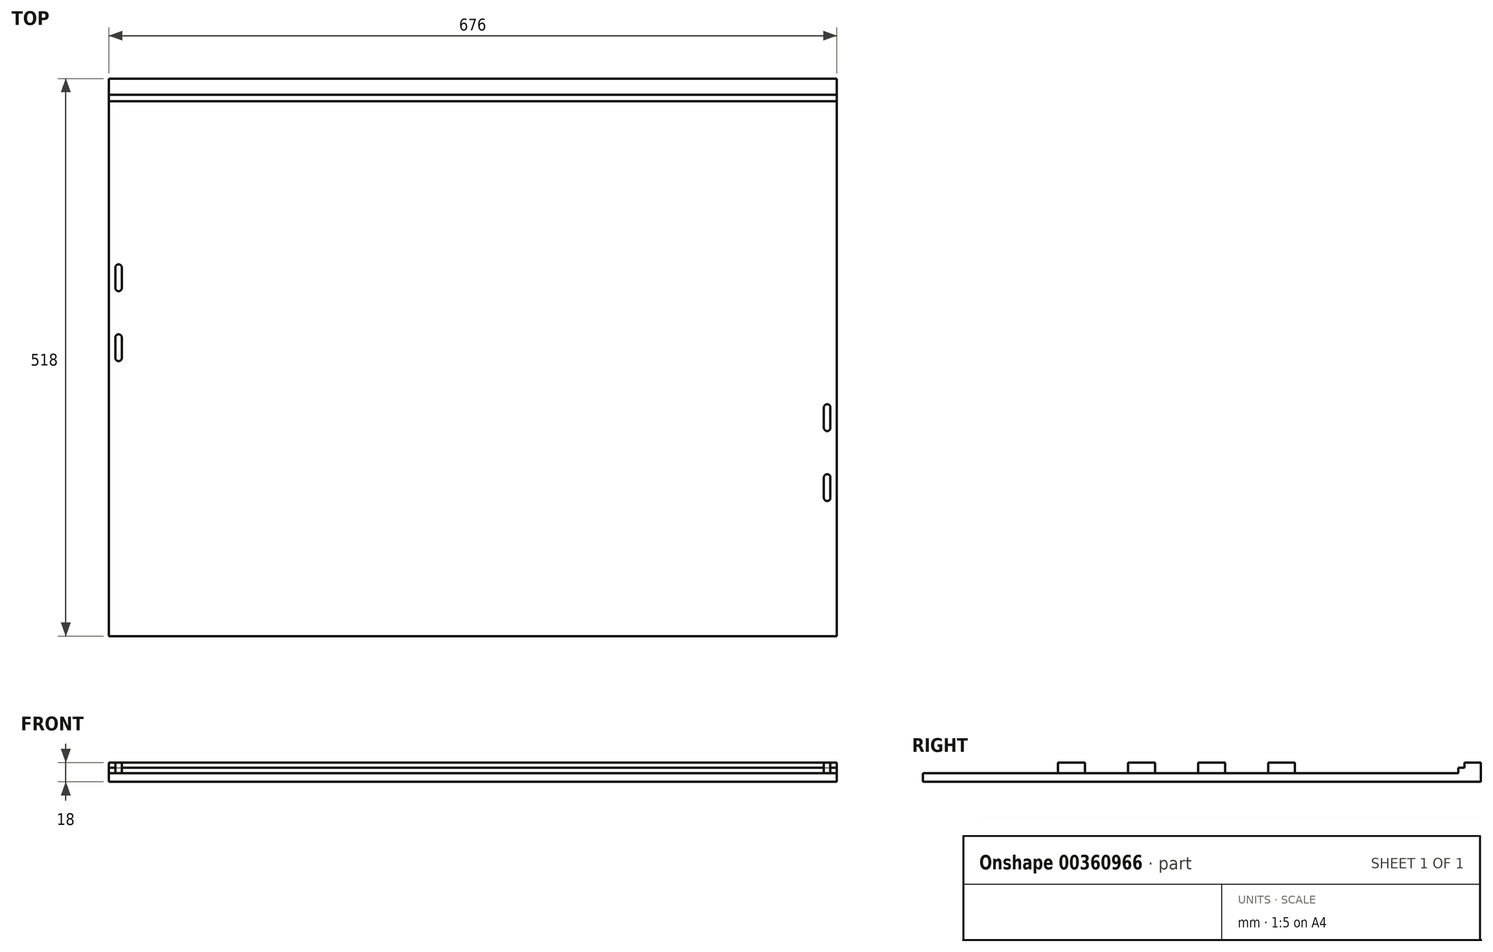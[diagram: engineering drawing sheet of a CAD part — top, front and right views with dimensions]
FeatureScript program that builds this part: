
annotation { "Feature Type Name" : "Feature", "Feature Type Description" : "" }
export const myFeature = defineFeature(function(context is Context, id is Id, definition is map)
    precondition{}
    {
        {
            var Q0;
            Q0=qCreatedBy(makeId("Top.planeOp"),FACE);
            var sketch = newSketch(context, id + "F0", { "sketchPlane" : qUnion([Q0])});
            skLineSegment(sketch, "E0.bottom", {"start": v(338, 250) * mm, "end": v(-338, 250) * mm});
            skLineSegment(sketch, "E0.top", {"start": v(338, -250) * mm, "end": v(-338, -250) * mm});
            skLineSegment(sketch, "E0.left", {"start": v(338, 250) * mm, "end": v(338, -250) * mm});
            skLineSegment(sketch, "E0.right", {"start": v(-338, 250) * mm, "end": v(-338, -250) * mm});
            skPoint(sketch, "E0.middle", {"position": v(0, 0) * mm});
            skSolve(sketch);
        }
        {
            var Q0;
            Q0=makeQuery(id+"F0.imprint","IMPRINT",FACE,{"disambiguationData":[TD([[makeQuery(id+"F0.imprint","IMPRINT",EDGE,{"derivedFrom":sQuery(id+"F0.wireOp",EDGE,"E0.bottom")}),1.0]])]});
            extrude(context, id + "F1", {"entities" : qUnion([Q0]), "depth" : 18 * mm});
        }
        {
            var Q0;
            Q0=makeQuery(id+"F1.opExtrude","CAP_FACE",FACE,{"disambiguationData":[OSD([sQuery(id+"F0.wireOp",EDGE,"E0.bottom"),sQuery(id+"F0.wireOp",EDGE,"E0.top"),sQuery(id+"F0.wireOp",EDGE,"E0.left"),sQuery(id+"F0.wireOp",EDGE,"E0.right")])],"isStart":false});
            var sketch = newSketch(context, id + "F2", { "sketchPlane" : qUnion([Q0])});
            skLineSegment(sketch, "E1.bottom", {"start": v(-338, 235) * mm, "end": v(338, 235) * mm});
            skLineSegment(sketch, "E1.top", {"start": v(-338, 229) * mm, "end": v(338, 229) * mm});
            skLineSegment(sketch, "E1.left", {"start": v(-338, 235) * mm, "end": v(-338, 229) * mm});
            skLineSegment(sketch, "E1.right", {"start": v(338, 235) * mm, "end": v(338, 229) * mm});
            skSolve(sketch);
        }
        {
            var Q0;
            Q0=makeQuery(id+"F2.imprint","IMPRINT",FACE,{"disambiguationData":[TD([[makeQuery(id+"F2.imprint","IMPRINT",EDGE,{"derivedFrom":sQuery(id+"F2.wireOp",EDGE,"E1.bottom")}),-1.0]])]});
            extrude(context, id + "F3", {"entities" : qUnion([Q0]), "operationType" : NewBodyOperationType.REMOVE, "oppositeDirection" : true, "depth" : 5 * mm});
        }
        {
            var Q0;
            {var subQ0=sQuery(id+"F0.wireOp",EDGE,"E0.top");var subQ1=sQuery(id+"F0.wireOp",EDGE,"E0.left");var subQ2=sQuery(id+"F0.wireOp",EDGE,"E0.right");Q0=makeQuery(id+"F3.boolean.opBoolean","SPLIT",FACE,{"disambiguationData":[TD([makeQuery(id+"F1.opExtrude","SWEPT_FACE",FACE,{"disambiguationData":[OSD([subQ0])]})])],"derivedFrom":makeQuery(id+"F1.opExtrude","CAP_FACE",FACE,{"disambiguationData":[OSD([sQuery(id+"F0.wireOp",EDGE,"E0.bottom"),subQ0,subQ1,subQ2])],"isStart":false})});}
            var sketch = newSketch(context, id + "F4", { "sketchPlane" : qUnion([Q0])});
            skLineSegment(sketch, "E2", {"start": v(-338, 0) * mm, "end": v(338, 0) * mm, "construction": true});
            skLineSegment(sketch, "E3.0", {"start": v(329, 224) * mm, "end": v(329, -250) * mm, "construction": true});
            skLineSegment(sketch, "E4.bottom", {"start": v(329, 12.5) * mm, "end": v(329, 12.5) * mm});
            skLineSegment(sketch, "E4.top", {"start": v(329, -12.5) * mm, "end": v(329, -12.5) * mm});
            skLineSegment(sketch, "E4.left", {"start": v(332, 9.5) * mm, "end": v(332, -9.5) * mm});
            skLineSegment(sketch, "E4.right", {"start": v(326, 9.5) * mm, "end": v(326, -9.5) * mm});
            skPoint(sketch, "E4.middle", {"position": v(329, 0) * mm});
            skPoint(sketch, "E5.visualSharp", {"position": v(326, 12.5) * mm});
            skArc(sketch, "E5.filletArc", {"start": v(329, 12.5) * mm, "mid": v(326.88, 11.62) * mm, "end": v(326, 9.5) * mm});
            skPoint(sketch, "E6.visualSharp", {"position": v(332, 12.5) * mm});
            skArc(sketch, "E6.filletArc", {"start": v(332, 9.5) * mm, "mid": v(331.12, 11.62) * mm, "end": v(329, 12.5) * mm});
            skPoint(sketch, "E7.visualSharp", {"position": v(326, -12.5) * mm});
            skArc(sketch, "E7.filletArc", {"start": v(326, -9.5) * mm, "mid": v(326.88, -11.62) * mm, "end": v(329, -12.5) * mm});
            skPoint(sketch, "E8.visualSharp", {"position": v(332, -12.5) * mm});
            skArc(sketch, "E8.filletArc", {"start": v(329, -12.5) * mm, "mid": v(331.12, -11.62) * mm, "end": v(332, -9.5) * mm});
            skLineSegment(sketch, "E9", {"start": v(0, -250) * mm, "end": v(0, 229) * mm, "construction": true});
            skLineSegment(sketch, "E10.0.1.0", {"start": v(326, 74.5) * mm, "end": v(326, 55.5) * mm});
            skLineSegment(sketch, "E10.0.1.1", {"start": v(332, 74.5) * mm, "end": v(332, 55.5) * mm});
            skPoint(sketch, "E10.0.1.2", {"position": v(329, 65) * mm});
            skPoint(sketch, "E10.0.1.3", {"position": v(326, 77.5) * mm});
            skPoint(sketch, "E10.0.1.4", {"position": v(332, 77.5) * mm});
            skPoint(sketch, "E10.0.1.5", {"position": v(332, 52.5) * mm});
            skPoint(sketch, "E10.0.1.6", {"position": v(326, 52.5) * mm});
            skArc(sketch, "E10.0.1.7", {"start": v(329, 52.5) * mm, "mid": v(331.12, 53.38) * mm, "end": v(332, 55.5) * mm});
            skArc(sketch, "E10.0.1.8", {"start": v(329, 77.5) * mm, "mid": v(326.88, 76.62) * mm, "end": v(326, 74.5) * mm});
            skArc(sketch, "E10.0.1.9", {"start": v(332, 74.5) * mm, "mid": v(331.12, 76.62) * mm, "end": v(329, 77.5) * mm});
            skArc(sketch, "E10.0.1.10", {"start": v(326, 55.5) * mm, "mid": v(326.88, 53.38) * mm, "end": v(329, 52.5) * mm});
            skLineSegment(sketch, "E10.0.2.0", {"start": v(326, 139.5) * mm, "end": v(326, 120.5) * mm});
            skLineSegment(sketch, "E10.0.2.1", {"start": v(332, 139.5) * mm, "end": v(332, 120.5) * mm});
            skPoint(sketch, "E10.0.2.2", {"position": v(329, 130) * mm});
            skPoint(sketch, "E10.0.2.3", {"position": v(326, 142.5) * mm});
            skPoint(sketch, "E10.0.2.4", {"position": v(332, 142.5) * mm});
            skPoint(sketch, "E10.0.2.5", {"position": v(332, 117.5) * mm});
            skPoint(sketch, "E10.0.2.6", {"position": v(326, 117.5) * mm});
            skArc(sketch, "E10.0.2.7", {"start": v(329, 117.5) * mm, "mid": v(331.12, 118.38) * mm, "end": v(332, 120.5) * mm});
            skArc(sketch, "E10.0.2.8", {"start": v(329, 142.5) * mm, "mid": v(326.88, 141.62) * mm, "end": v(326, 139.5) * mm});
            skArc(sketch, "E10.0.2.9", {"start": v(332, 139.5) * mm, "mid": v(331.12, 141.62) * mm, "end": v(329, 142.5) * mm});
            skArc(sketch, "E10.0.2.10", {"start": v(326, 120.5) * mm, "mid": v(326.88, 118.38) * mm, "end": v(329, 117.5) * mm});
            skLineSegment(sketch, "E10.0.3.0", {"start": v(326, 204.5) * mm, "end": v(326, 185.5) * mm});
            skLineSegment(sketch, "E10.0.3.1", {"start": v(332, 204.5) * mm, "end": v(332, 185.5) * mm});
            skPoint(sketch, "E10.0.3.2", {"position": v(329, 195) * mm});
            skPoint(sketch, "E10.0.3.3", {"position": v(326, 207.5) * mm});
            skPoint(sketch, "E10.0.3.4", {"position": v(332, 207.5) * mm});
            skPoint(sketch, "E10.0.3.5", {"position": v(332, 182.5) * mm});
            skPoint(sketch, "E10.0.3.6", {"position": v(326, 182.5) * mm});
            skArc(sketch, "E10.0.3.7", {"start": v(329, 182.5) * mm, "mid": v(331.12, 183.38) * mm, "end": v(332, 185.5) * mm});
            skArc(sketch, "E10.0.3.8", {"start": v(329, 207.5) * mm, "mid": v(326.88, 206.62) * mm, "end": v(326, 204.5) * mm});
            skArc(sketch, "E10.0.3.9", {"start": v(332, 204.5) * mm, "mid": v(331.12, 206.62) * mm, "end": v(329, 207.5) * mm});
            skArc(sketch, "E10.0.3.10", {"start": v(326, 185.5) * mm, "mid": v(326.88, 183.38) * mm, "end": v(329, 182.5) * mm});
            skLineSegment(sketch, "E10.direction1", {"start": v(326, -12.5) * mm, "end": v(353, -12.5) * mm, "construction": true});
            skLineSegment(sketch, "E10.direction2", {"start": v(326, -12.5) * mm, "end": v(326, 52.5) * mm, "construction": true});
            skArc(sketch, "E11.MirrorCS", {"start": v(329, -117.5) * mm, "mid": v(331.12, -118.38) * mm, "end": v(332, -120.5) * mm});
            skArc(sketch, "E12.MirrorCS", {"start": v(326, -120.5) * mm, "mid": v(326.88, -118.38) * mm, "end": v(329, -117.5) * mm});
            skLineSegment(sketch, "E13.MirrorCS", {"start": v(326, -204.5) * mm, "end": v(326, -185.5) * mm});
            skArc(sketch, "E14.MirrorCS", {"start": v(329, -207.5) * mm, "mid": v(326.88, -206.62) * mm, "end": v(326, -204.5) * mm});
            skArc(sketch, "E15.MirrorCS", {"start": v(329, -77.5) * mm, "mid": v(326.88, -76.62) * mm, "end": v(326, -74.5) * mm});
            skArc(sketch, "E16.MirrorCS", {"start": v(329, -52.5) * mm, "mid": v(331.12, -53.38) * mm, "end": v(332, -55.5) * mm});
            skLineSegment(sketch, "E17.MirrorCS", {"start": v(332, -74.5) * mm, "end": v(332, -55.5) * mm});
            skLineSegment(sketch, "E18.MirrorCS", {"start": v(326, -74.5) * mm, "end": v(326, -55.5) * mm});
            skArc(sketch, "E19.MirrorCS", {"start": v(329, -182.5) * mm, "mid": v(331.12, -183.38) * mm, "end": v(332, -185.5) * mm});
            skLineSegment(sketch, "E20.MirrorCS", {"start": v(326, -139.5) * mm, "end": v(326, -120.5) * mm});
            skArc(sketch, "E21.MirrorCS", {"start": v(326, -55.5) * mm, "mid": v(326.88, -53.38) * mm, "end": v(329, -52.5) * mm});
            skArc(sketch, "E22.MirrorCS", {"start": v(332, -74.5) * mm, "mid": v(331.12, -76.62) * mm, "end": v(329, -77.5) * mm});
            skArc(sketch, "E23.MirrorCS", {"start": v(326, -185.5) * mm, "mid": v(326.88, -183.38) * mm, "end": v(329, -182.5) * mm});
            skArc(sketch, "E24.MirrorCS", {"start": v(332, -139.5) * mm, "mid": v(331.12, -141.62) * mm, "end": v(329, -142.5) * mm});
            skArc(sketch, "E25.MirrorCS", {"start": v(329, -142.5) * mm, "mid": v(326.88, -141.62) * mm, "end": v(326, -139.5) * mm});
            skLineSegment(sketch, "E26.MirrorCS", {"start": v(332, -204.5) * mm, "end": v(332, -185.5) * mm});
            skLineSegment(sketch, "E27.MirrorCS", {"start": v(332, -139.5) * mm, "end": v(332, -120.5) * mm});
            skArc(sketch, "E28.MirrorCS", {"start": v(332, -204.5) * mm, "mid": v(331.12, -206.62) * mm, "end": v(329, -207.5) * mm});
            skPoint(sketch, "E29.MirrorP", {"position": v(332, -52.5) * mm});
            skPoint(sketch, "E30.MirrorP", {"position": v(326, -207.5) * mm});
            skPoint(sketch, "E31.MirrorP", {"position": v(332, -117.5) * mm});
            skPoint(sketch, "E32.MirrorP", {"position": v(329, -130) * mm});
            skPoint(sketch, "E33.MirrorP", {"position": v(332, -182.5) * mm});
            skPoint(sketch, "E34.MirrorP", {"position": v(332, -77.5) * mm});
            skPoint(sketch, "E35.MirrorP", {"position": v(329, -195) * mm});
            skPoint(sketch, "E36.MirrorP", {"position": v(332, -142.5) * mm});
            skPoint(sketch, "E37.MirrorP", {"position": v(326, -52.5) * mm});
            skPoint(sketch, "E38.MirrorP", {"position": v(329, -65) * mm});
            skPoint(sketch, "E39.MirrorP", {"position": v(326, -182.5) * mm});
            skPoint(sketch, "E40.MirrorP", {"position": v(332, -207.5) * mm});
            skPoint(sketch, "E41.MirrorP", {"position": v(326, -117.5) * mm});
            skPoint(sketch, "E42.MirrorP", {"position": v(326, -77.5) * mm});
            skPoint(sketch, "E43.MirrorP", {"position": v(326, -142.5) * mm});
            skArc(sketch, "E44.MirrorCS", {"start": v(-329, -117.5) * mm, "mid": v(-331.12, -118.38) * mm, "end": v(-332, -120.5) * mm});
            skArc(sketch, "E45.MirrorCS", {"start": v(-326, -120.5) * mm, "mid": v(-326.88, -118.38) * mm, "end": v(-329, -117.5) * mm});
            skArc(sketch, "E46.MirrorCS", {"start": v(-329, -12.5) * mm, "mid": v(-331.12, -11.62) * mm, "end": v(-332, -9.5) * mm});
            skArc(sketch, "E47.MirrorCS", {"start": v(-326, -9.5) * mm, "mid": v(-326.88, -11.62) * mm, "end": v(-329, -12.5) * mm});
            skArc(sketch, "E48.MirrorCS", {"start": v(-332, 9.5) * mm, "mid": v(-331.12, 11.62) * mm, "end": v(-329, 12.5) * mm});
            skLineSegment(sketch, "E49.MirrorCS", {"start": v(-326, 9.5) * mm, "end": v(-326, -9.5) * mm});
            skArc(sketch, "E50.MirrorCS", {"start": v(-329, 12.5) * mm, "mid": v(-326.88, 11.62) * mm, "end": v(-326, 9.5) * mm});
            skLineSegment(sketch, "E51.MirrorCS", {"start": v(-332, 9.5) * mm, "end": v(-332, -9.5) * mm});
            skLineSegment(sketch, "E52.MirrorCS", {"start": v(-326, -204.5) * mm, "end": v(-326, -185.5) * mm});
            skLineSegment(sketch, "E53.MirrorCS", {"start": v(-332, 204.5) * mm, "end": v(-332, 185.5) * mm});
            skArc(sketch, "E54.MirrorCS", {"start": v(-329, -207.5) * mm, "mid": v(-326.88, -206.62) * mm, "end": v(-326, -204.5) * mm});
            skLineSegment(sketch, "E55.MirrorCS", {"start": v(-332, 139.5) * mm, "end": v(-332, 120.5) * mm});
            skArc(sketch, "E56.MirrorCS", {"start": v(-329, 182.5) * mm, "mid": v(-331.12, 183.38) * mm, "end": v(-332, 185.5) * mm});
            skArc(sketch, "E57.MirrorCS", {"start": v(-326, -55.5) * mm, "mid": v(-326.88, -53.38) * mm, "end": v(-329, -52.5) * mm});
            skArc(sketch, "E58.MirrorCS", {"start": v(-329, 207.5) * mm, "mid": v(-326.88, 206.62) * mm, "end": v(-326, 204.5) * mm});
            skArc(sketch, "E59.MirrorCS", {"start": v(-329, 117.5) * mm, "mid": v(-331.12, 118.38) * mm, "end": v(-332, 120.5) * mm});
            skArc(sketch, "E60.MirrorCS", {"start": v(-326, -185.5) * mm, "mid": v(-326.88, -183.38) * mm, "end": v(-329, -182.5) * mm});
            skArc(sketch, "E61.MirrorCS", {"start": v(-332, 204.5) * mm, "mid": v(-331.12, 206.62) * mm, "end": v(-329, 207.5) * mm});
            skArc(sketch, "E62.MirrorCS", {"start": v(-329, -52.5) * mm, "mid": v(-331.12, -53.38) * mm, "end": v(-332, -55.5) * mm});
            skArc(sketch, "E63.MirrorCS", {"start": v(-329, 142.5) * mm, "mid": v(-326.88, 141.62) * mm, "end": v(-326, 139.5) * mm});
            skArc(sketch, "E64.MirrorCS", {"start": v(-326, 185.5) * mm, "mid": v(-326.88, 183.38) * mm, "end": v(-329, 182.5) * mm});
            skArc(sketch, "E65.MirrorCS", {"start": v(-332, -204.5) * mm, "mid": v(-331.12, -206.62) * mm, "end": v(-329, -207.5) * mm});
            skLineSegment(sketch, "E66.MirrorCS", {"start": v(-326, 204.5) * mm, "end": v(-326, 185.5) * mm});
            skArc(sketch, "E67.MirrorCS", {"start": v(-329, -182.5) * mm, "mid": v(-331.12, -183.38) * mm, "end": v(-332, -185.5) * mm});
            skLineSegment(sketch, "E68.MirrorCS", {"start": v(-332, -204.5) * mm, "end": v(-332, -185.5) * mm});
            skLineSegment(sketch, "E69.MirrorCS", {"start": v(-326, 139.5) * mm, "end": v(-326, 120.5) * mm});
            skArc(sketch, "E70.MirrorCS", {"start": v(-332, 139.5) * mm, "mid": v(-331.12, 141.62) * mm, "end": v(-329, 142.5) * mm});
            skArc(sketch, "E71.MirrorCS", {"start": v(-326, 120.5) * mm, "mid": v(-326.88, 118.38) * mm, "end": v(-329, 117.5) * mm});
            skLineSegment(sketch, "E72.MirrorCS", {"start": v(-326, -139.5) * mm, "end": v(-326, -120.5) * mm});
            skArc(sketch, "E73.MirrorCS", {"start": v(-332, -74.5) * mm, "mid": v(-331.12, -76.62) * mm, "end": v(-329, -77.5) * mm});
            skArc(sketch, "E74.MirrorCS", {"start": v(-329, -77.5) * mm, "mid": v(-326.88, -76.62) * mm, "end": v(-326, -74.5) * mm});
            skArc(sketch, "E75.MirrorCS", {"start": v(-332, -139.5) * mm, "mid": v(-331.12, -141.62) * mm, "end": v(-329, -142.5) * mm});
            skLineSegment(sketch, "E76.MirrorCS", {"start": v(-332, -74.5) * mm, "end": v(-332, -55.5) * mm});
            skLineSegment(sketch, "E77.MirrorCS", {"start": v(-326, -74.5) * mm, "end": v(-326, -55.5) * mm});
            skArc(sketch, "E78.MirrorCS", {"start": v(-329, -142.5) * mm, "mid": v(-326.88, -141.62) * mm, "end": v(-326, -139.5) * mm});
            skArc(sketch, "E79.MirrorCS", {"start": v(-329, 77.5) * mm, "mid": v(-326.88, 76.62) * mm, "end": v(-326, 74.5) * mm});
            skArc(sketch, "E80.MirrorCS", {"start": v(-329, 52.5) * mm, "mid": v(-331.12, 53.38) * mm, "end": v(-332, 55.5) * mm});
            skLineSegment(sketch, "E81.MirrorCS", {"start": v(-332, 74.5) * mm, "end": v(-332, 55.5) * mm});
            skLineSegment(sketch, "E82.MirrorCS", {"start": v(-326, 74.5) * mm, "end": v(-326, 55.5) * mm});
            skLineSegment(sketch, "E83.MirrorCS", {"start": v(-332, -139.5) * mm, "end": v(-332, -120.5) * mm});
            skArc(sketch, "E84.MirrorCS", {"start": v(-332, 74.5) * mm, "mid": v(-331.12, 76.62) * mm, "end": v(-329, 77.5) * mm});
            skArc(sketch, "E85.MirrorCS", {"start": v(-326, 55.5) * mm, "mid": v(-326.88, 53.38) * mm, "end": v(-329, 52.5) * mm});
            skPoint(sketch, "E86.MirrorP", {"position": v(-329, 65) * mm});
            skPoint(sketch, "E87.MirrorP", {"position": v(-329, -65) * mm});
            skPoint(sketch, "E88.MirrorP", {"position": v(-329, 130) * mm});
            skPoint(sketch, "E89.MirrorP", {"position": v(-329, 195) * mm});
            skLineSegment(sketch, "E90.MirrorCS", {"start": v(-326, -12.5) * mm, "end": v(-326, 52.5) * mm, "construction": true});
            skLineSegment(sketch, "E91.MirrorCS", {"start": v(-326, -12.5) * mm, "end": v(-353, -12.5) * mm, "construction": true});
            skPoint(sketch, "E92.MirrorP", {"position": v(-329, 0) * mm});
            skPoint(sketch, "E93.MirrorP", {"position": v(-332, -12.5) * mm});
            skPoint(sketch, "E94.MirrorP", {"position": v(-332, -117.5) * mm});
            skPoint(sketch, "E95.MirrorP", {"position": v(-326, 77.5) * mm});
            skPoint(sketch, "E96.MirrorP", {"position": v(-326, -182.5) * mm});
            skPoint(sketch, "E97.MirrorP", {"position": v(-329, -130) * mm});
            skPoint(sketch, "E98.MirrorP", {"position": v(-326, 142.5) * mm});
            skPoint(sketch, "E99.MirrorP", {"position": v(-332, 12.5) * mm});
            skPoint(sketch, "E100.MirrorP", {"position": v(-332, -207.5) * mm});
            skPoint(sketch, "E101.MirrorP", {"position": v(-332, -182.5) * mm});
            skPoint(sketch, "E102.MirrorP", {"position": v(-332, 142.5) * mm});
            skPoint(sketch, "E103.MirrorP", {"position": v(-332, 77.5) * mm});
            skPoint(sketch, "E104.MirrorP", {"position": v(-332, -77.5) * mm});
            skPoint(sketch, "E105.MirrorP", {"position": v(-332, 117.5) * mm});
            skPoint(sketch, "E106.MirrorP", {"position": v(-326, -12.5) * mm});
            skPoint(sketch, "E107.MirrorP", {"position": v(-326, 12.5) * mm});
            skPoint(sketch, "E108.MirrorP", {"position": v(-326, -207.5) * mm});
            skPoint(sketch, "E109.MirrorP", {"position": v(-326, -52.5) * mm});
            skPoint(sketch, "E110.MirrorP", {"position": v(-326, 117.5) * mm});
            skPoint(sketch, "E111.MirrorP", {"position": v(-326, 182.5) * mm});
            skPoint(sketch, "E112.MirrorP", {"position": v(-329, -195) * mm});
            skPoint(sketch, "E113.MirrorP", {"position": v(-326, -142.5) * mm});
            skPoint(sketch, "E114.MirrorP", {"position": v(-332, 182.5) * mm});
            skPoint(sketch, "E115.MirrorP", {"position": v(-326, -117.5) * mm});
            skPoint(sketch, "E116.MirrorP", {"position": v(-326, -77.5) * mm});
            skPoint(sketch, "E117.MirrorP", {"position": v(-326, 52.5) * mm});
            skPoint(sketch, "E118.MirrorP", {"position": v(-332, 207.5) * mm});
            skPoint(sketch, "E119.MirrorP", {"position": v(-332, 52.5) * mm});
            skPoint(sketch, "E120.MirrorP", {"position": v(-326, 207.5) * mm});
            skPoint(sketch, "E121.MirrorP", {"position": v(-332, -142.5) * mm});
            skPoint(sketch, "E122.MirrorP", {"position": v(-332, -52.5) * mm});
            skSolve(sketch);
        }
        {
            var Q0;
            Q0=makeQuery(id+"F4.imprint","IMPRINT",FACE,{"disambiguationData":[TD([[makeQuery(id+"F4.imprint","IMPRINT",EDGE,{"derivedFrom":sQuery(id+"F4.wireOp",EDGE,"E13.MirrorCS")}),-1.0]])]});
            var Q1;
            Q1=makeQuery(id+"F4.imprint","IMPRINT",FACE,{"disambiguationData":[TD([[makeQuery(id+"F4.imprint","IMPRINT",EDGE,{"derivedFrom":sQuery(id+"F4.wireOp",EDGE,"E11.MirrorCS")}),-1.0]])]});
            var Q2;
            Q2=makeQuery(id+"F4.imprint","IMPRINT",FACE,{"disambiguationData":[TD([[makeQuery(id+"F4.imprint","IMPRINT",EDGE,{"derivedFrom":sQuery(id+"F4.wireOp",EDGE,"E15.MirrorCS")}),-1.0]])]});
            var Q3;
            Q3=makeQuery(id+"F4.imprint","IMPRINT",FACE,{"disambiguationData":[TD([[makeQuery(id+"F4.imprint","IMPRINT",EDGE,{"derivedFrom":sQuery(id+"F4.wireOp",EDGE,"E4.left")}),-1.0]])]});
            var Q4;
            Q4=makeQuery(id+"F4.imprint","IMPRINT",FACE,{"disambiguationData":[TD([[makeQuery(id+"F4.imprint","IMPRINT",EDGE,{"derivedFrom":sQuery(id+"F4.wireOp",EDGE,"E10.0.1.0")}),1.0]])]});
            var Q5;
            Q5=makeQuery(id+"F4.imprint","IMPRINT",FACE,{"disambiguationData":[TD([[makeQuery(id+"F4.imprint","IMPRINT",EDGE,{"derivedFrom":sQuery(id+"F4.wireOp",EDGE,"E10.0.2.0")}),1.0]])]});
            var Q6;
            Q6=makeQuery(id+"F4.imprint","IMPRINT",FACE,{"disambiguationData":[TD([[makeQuery(id+"F4.imprint","IMPRINT",EDGE,{"derivedFrom":sQuery(id+"F4.wireOp",EDGE,"E10.0.3.0")}),1.0]])]});
            var Q7;
            Q7=makeQuery(id+"F4.imprint","IMPRINT",FACE,{"disambiguationData":[TD([[makeQuery(id+"F4.imprint","IMPRINT",EDGE,{"derivedFrom":sQuery(id+"F4.wireOp",EDGE,"E52.MirrorCS")}),1.0]])]});
            var Q8;
            Q8=makeQuery(id+"F4.imprint","IMPRINT",FACE,{"disambiguationData":[TD([[makeQuery(id+"F4.imprint","IMPRINT",EDGE,{"derivedFrom":sQuery(id+"F4.wireOp",EDGE,"E44.MirrorCS")}),1.0]])]});
            var Q9;
            Q9=makeQuery(id+"F4.imprint","IMPRINT",FACE,{"disambiguationData":[TD([[makeQuery(id+"F4.imprint","IMPRINT",EDGE,{"derivedFrom":sQuery(id+"F4.wireOp",EDGE,"E57.MirrorCS")}),1.0]])]});
            var Q10;
            Q10=makeQuery(id+"F4.imprint","IMPRINT",FACE,{"disambiguationData":[TD([[makeQuery(id+"F4.imprint","IMPRINT",EDGE,{"derivedFrom":sQuery(id+"F4.wireOp",EDGE,"E46.MirrorCS")}),-1.0]])]});
            var Q11;
            Q11=makeQuery(id+"F4.imprint","IMPRINT",FACE,{"disambiguationData":[TD([[makeQuery(id+"F4.imprint","IMPRINT",EDGE,{"derivedFrom":sQuery(id+"F4.wireOp",EDGE,"E79.MirrorCS")}),-1.0]])]});
            var Q12;
            Q12=makeQuery(id+"F4.imprint","IMPRINT",FACE,{"disambiguationData":[TD([[makeQuery(id+"F4.imprint","IMPRINT",EDGE,{"derivedFrom":sQuery(id+"F4.wireOp",EDGE,"E55.MirrorCS")}),1.0]])]});
            var Q13;
            Q13=makeQuery(id+"F4.imprint","IMPRINT",FACE,{"disambiguationData":[TD([[makeQuery(id+"F4.imprint","IMPRINT",EDGE,{"derivedFrom":sQuery(id+"F4.wireOp",EDGE,"E53.MirrorCS")}),1.0]])]});
            extrude(context, id + "F5", {"entities" : qUnion([Q0, Q1, Q2, Q3, Q4, Q5, Q6, Q7, Q8, Q9, Q10, Q11, Q12, Q13]), "operationType" : NewBodyOperationType.REMOVE, "oppositeDirection" : true, "depth" : 10 * mm});
        }
        {
            var Q0;
            Q0=makeQuery(id+"F1.opExtrude","SWEPT_FACE",FACE,{"disambiguationData":[OSD([sQuery(id+"F0.wireOp",EDGE,"E0.top")])]});
            extrude(context, id + "F6", {"entities" : qUnion([Q0]), "operationType" : NewBodyOperationType.ADD, "depth" : 18 * mm});
        }
    });
